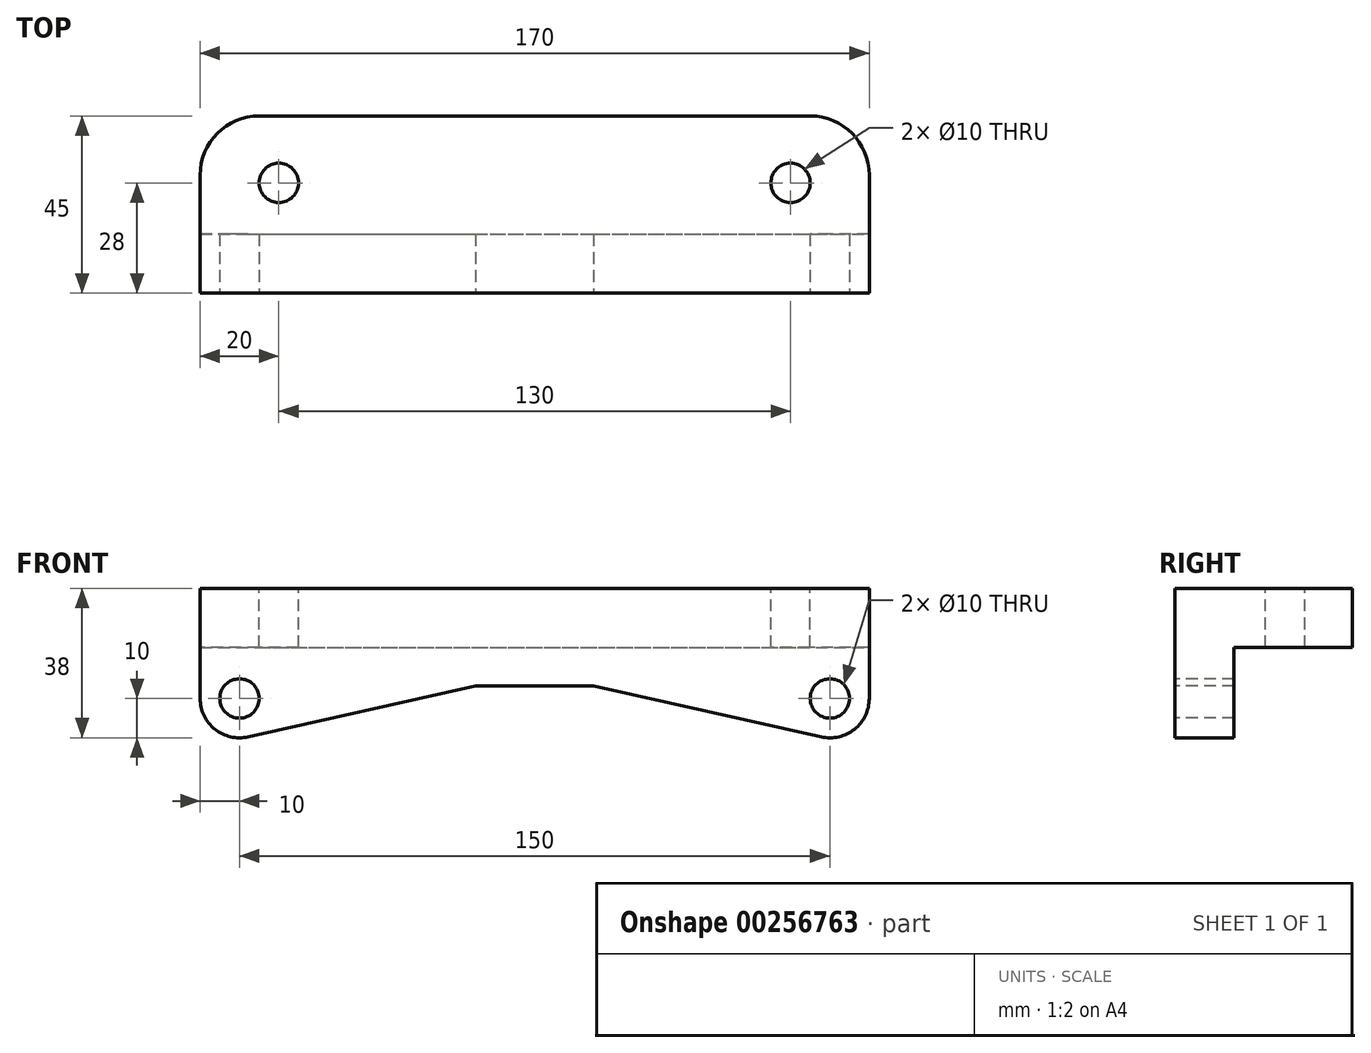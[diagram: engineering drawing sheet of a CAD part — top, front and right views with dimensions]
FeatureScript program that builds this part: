
annotation { "Feature Type Name" : "Feature", "Feature Type Description" : "" }
export const myFeature = defineFeature(function(context is Context, id is Id, definition is map)
    precondition{}
    {
        {
            var Q0;
            Q0=qCreatedBy(makeId("Top.planeOp"),FACE);
            var sketch = newSketch(context, id + "F0", { "sketchPlane" : qUnion([Q0])});
            skLineSegment(sketch, "E0.bottom", {"start": v(-85, 22.5) * mm, "end": v(85, 22.5) * mm});
            skLineSegment(sketch, "E0.top", {"start": v(-85, -22.5) * mm, "end": v(85, -22.5) * mm});
            skLineSegment(sketch, "E0.left", {"start": v(-85, 22.5) * mm, "end": v(-85, -22.5) * mm});
            skLineSegment(sketch, "E0.right", {"start": v(85, 22.5) * mm, "end": v(85, -22.5) * mm});
            skPoint(sketch, "E0.middle", {"position": v(0, 0) * mm});
            skSolve(sketch);
        }
        {
            var Q0;
            Q0=makeQuery(id+"F0.imprint","IMPRINT",FACE,{"disambiguationData":[TD([[makeQuery(id+"F0.imprint","IMPRINT",EDGE,{"derivedFrom":sQuery(id+"F0.wireOp",EDGE,"E0.bottom")}),-1.0]])]});
            extrude(context, id + "F1", {"entities" : qUnion([Q0]), "depth" : 52.5 * mm});
        }
        {
            var Q0;
            Q0=makeQuery(id+"F1.opExtrude","CAP_FACE",FACE,{"disambiguationData":[OSD([sQuery(id+"F0.wireOp",EDGE,"E0.bottom"),sQuery(id+"F0.wireOp",EDGE,"E0.top"),sQuery(id+"F0.wireOp",EDGE,"E0.left"),sQuery(id+"F0.wireOp",EDGE,"E0.right")])],"isStart":false});
            var sketch = newSketch(context, id + "F2", { "sketchPlane" : qUnion([Q0])});
            skLineSegment(sketch, "E1", {"start": v(-65, 5.5) * mm, "end": v(65, 5.5) * mm});
            skSolve(sketch);
        }
        {
            var Q0;
            Q0=sQuery(id+"F2.wireOp",VERTEX,"E1.start");
            var Q1;
            Q1=sQuery(id+"F2.wireOp",VERTEX,"E1.end");
            var Q2;
            Q2=makeQuery(id+"F1.opExtrude","SWEPT_BODY",BODY,{"disambiguationData":[OSD([sQuery(id+"F0.wireOp",EDGE,"E0.bottom"),sQuery(id+"F0.wireOp",EDGE,"E0.top"),sQuery(id+"F0.wireOp",EDGE,"E0.left"),sQuery(id+"F0.wireOp",EDGE,"E0.right")])]});
            hole(context, id + "F3", {"style" : HoleStyle.SIMPLE, "endStyle" : HoleEndStyle.THROUGH, "holeDiameter" : 10 * mm, "tappedDepth" : 12 * mm, "tapClearance" : 3, "startFromSketch" : true, "locations" : qUnion([Q0, Q1]), "scope" : qUnion([Q2])});
        }
        {
            var Q0;
            Q0=makeQuery(id+"F1.opExtrude","SWEPT_FACE",FACE,{"disambiguationData":[OSD([sQuery(id+"F0.wireOp",EDGE,"E0.top")])]});
            var sketch = newSketch(context, id + "F4", { "sketchPlane" : qUnion([Q0])});
            skArc(sketch, "E2", {"start": v(85, 0) * mm, "mid": v(0, 27.5) * mm, "end": v(-85, 0) * mm});
            skLineSegment(sketch, "E3", {"start": v(-85, 0) * mm, "end": v(85, 0) * mm});
            skSolve(sketch);
        }
        {
            var Q0;
            Q0=makeQuery(id+"F4.imprint","IMPRINT",FACE,{"disambiguationData":[TD([[makeQuery(id+"F4.imprint","IMPRINT",EDGE,{"derivedFrom":sQuery(id+"F4.wireOp",EDGE,"E2")}),1.0]])]});
            extrude(context, id + "F5", {"entities" : qUnion([Q0]), "operationType" : NewBodyOperationType.REMOVE, "endBound" : BoundingType.THROUGH_ALL, "oppositeDirection" : true, "depth" : 25 * mm});
        }
        {
            var Q0;
            Q0=makeQuery(id+"F1.opExtrude","SWEPT_FACE",FACE,{"disambiguationData":[OSD([sQuery(id+"F0.wireOp",EDGE,"E0.right")])]});
            var sketch = newSketch(context, id + "F6", { "sketchPlane" : qUnion([Q0])});
            skLineSegment(sketch, "E4.bottom", {"start": v(22.5, 0) * mm, "end": v(-7.5, 0) * mm});
            skLineSegment(sketch, "E4.top", {"start": v(22.5, 37.5) * mm, "end": v(-7.5, 37.5) * mm});
            skLineSegment(sketch, "E4.left", {"start": v(22.5, 0) * mm, "end": v(22.5, 37.5) * mm});
            skLineSegment(sketch, "E4.right", {"start": v(-7.5, 0) * mm, "end": v(-7.5, 37.5) * mm});
            skSolve(sketch);
        }
        {
            var Q0;
            Q0=makeQuery(id+"F6.imprint","IMPRINT",FACE,{"disambiguationData":[TD([[makeQuery(id+"F6.imprint","IMPRINT",EDGE,{"derivedFrom":sQuery(id+"F6.wireOp",EDGE,"E4.bottom")}),-1.0]])]});
            extrude(context, id + "F7", {"entities" : qUnion([Q0]), "operationType" : NewBodyOperationType.REMOVE, "endBound" : BoundingType.THROUGH_ALL, "oppositeDirection" : true, "depth" : 25 * mm});
        }
        {
            var Q0;
            Q0=makeQuery(id+"F1.opExtrude","SWEPT_FACE",FACE,{"disambiguationData":[OSD([sQuery(id+"F0.wireOp",EDGE,"E0.top")])]});
            var sketch = newSketch(context, id + "F8", { "sketchPlane" : qUnion([Q0])});
            skLineSegment(sketch, "E5", {"start": v(-75, 24.5) * mm, "end": v(75, 24.5) * mm});
            skLineSegment(sketch, "E6", {"start": v(0, 0) * mm, "end": v(0, 24.5) * mm});
            skSolve(sketch);
        }
        {
            var Q0;
            Q0=sQuery(id+"F8.wireOp",VERTEX,"E5.start");
            var Q1;
            Q1=sQuery(id+"F8.wireOp",VERTEX,"E5.end");
            var Q2;
            Q2=makeQuery(id+"F1.opExtrude","SWEPT_BODY",BODY,{"disambiguationData":[OSD([sQuery(id+"F0.wireOp",EDGE,"E0.bottom"),sQuery(id+"F0.wireOp",EDGE,"E0.top"),sQuery(id+"F0.wireOp",EDGE,"E0.left"),sQuery(id+"F0.wireOp",EDGE,"E0.right")])]});
            hole(context, id + "F9", {"style" : HoleStyle.SIMPLE, "endStyle" : HoleEndStyle.THROUGH, "holeDiameter" : 10 * mm, "tappedDepth" : 12 * mm, "tapClearance" : 3, "startFromSketch" : true, "locations" : qUnion([Q0, Q1]), "scope" : qUnion([Q2])});
        }
        {
            var Q0;
            Q0=makeQuery(id+"F1.opExtrude","SWEPT_FACE",FACE,{"disambiguationData":[OSD([sQuery(id+"F0.wireOp",EDGE,"E0.top")])]});
            var sketch = newSketch(context, id + "F10", { "sketchPlane" : qUnion([Q0])});
            skArc(sketch, "E7", {"start": v(-85, 24.5) * mm, "mid": v(-81.25, 16.7) * mm, "end": v(-72.8, 14.74) * mm});
            skLineSegment(sketch, "E8", {"start": v(-72.8, 14.74) * mm, "end": v(-31.86, 23.96) * mm});
            skLineSegment(sketch, "E9", {"start": v(-85, 24.5) * mm, "end": v(-85, 0) * mm});
            skLineSegment(sketch, "E10", {"start": v(-85, 0) * mm, "end": v(-31.86, 23.96) * mm});
            skArc(sketch, "E11", {"start": v(72.8, 14.74) * mm, "mid": v(81.25, 16.7) * mm, "end": v(85, 24.5) * mm});
            skLineSegment(sketch, "E12", {"start": v(72.8, 14.74) * mm, "end": v(31.86, 23.96) * mm});
            skLineSegment(sketch, "E13", {"start": v(85, 24.5) * mm, "end": v(85, 0) * mm});
            skLineSegment(sketch, "E14", {"start": v(85, 0) * mm, "end": v(31.86, 23.96) * mm});
            skSolve(sketch);
        }
        {
            var Q0;
            Q0=makeQuery(id+"F10.imprint","IMPRINT",FACE,{"disambiguationData":[TD([[makeQuery(id+"F10.imprint","IMPRINT",EDGE,{"derivedFrom":sQuery(id+"F10.wireOp",EDGE,"E11")}),-1.0]])]});
            var Q1;
            Q1=makeQuery(id+"F10.imprint","IMPRINT",FACE,{"disambiguationData":[TD([[makeQuery(id+"F10.imprint","IMPRINT",EDGE,{"derivedFrom":sQuery(id+"F10.wireOp",EDGE,"E7")}),-1.0]])]});
            extrude(context, id + "F11", {"entities" : qUnion([Q0, Q1]), "operationType" : NewBodyOperationType.REMOVE, "endBound" : BoundingType.THROUGH_ALL, "oppositeDirection" : true, "depth" : 25 * mm});
        }
        {
            var Q0;
            Q0=makeQuery(id+"F1.opExtrude","SWEPT_EDGE",EDGE,{"disambiguationData":[OSD([sQuery(id+"F0.wireOp",EDGE,"E0.bottom"),sQuery(id+"F0.wireOp",EDGE,"E0.right")])]});
            var Q1;
            Q1=makeQuery(id+"F1.opExtrude","SWEPT_EDGE",EDGE,{"disambiguationData":[OSD([sQuery(id+"F0.wireOp",EDGE,"E0.bottom"),sQuery(id+"F0.wireOp",EDGE,"E0.left")])]});
            fillet(context, id + "F12", {"entities" : qUnion([Q0, Q1]), "radius" : 15 * mm, "tangentPropagation" : true, "allowEdgeOverflow" : false});
        }
        {
            var Q0;
            Q0=makeQuery(id+"F1.opExtrude","SWEPT_FACE",FACE,{"disambiguationData":[OSD([sQuery(id+"F0.wireOp",EDGE,"E0.top")])]});
            var sketch = newSketch(context, id + "F13", { "sketchPlane" : qUnion([Q0])});
            skLineSegment(sketch, "E15", {"start": v(-72.8, 14.74) * mm, "end": v(-48.97, 34.74) * mm});
            skLineSegment(sketch, "E16", {"start": v(-48.97, 34.74) * mm, "end": v(48.97, 34.74) * mm});
            skLineSegment(sketch, "E17", {"start": v(48.97, 34.74) * mm, "end": v(72.8, 14.74) * mm});
            skLineSegment(sketch, "E18", {"start": v(72.8, 14.74) * mm, "end": v(-72.8, 14.74) * mm});
            skSolve(sketch);
        }
        {
            var Q0;
            Q0 = qSketchRegion(id + "F13", true);
            var Q1;
            Q1=makeQuery(id+"F7.boolean.opBoolean","COPY",FACE,{"derivedFrom":makeQuery(id+"F7.opExtrude","SWEPT_FACE",FACE,{"disambiguationData":[OSD([sQuery(id+"F6.wireOp",EDGE,"E4.right")])]})});
            extrude(context, id + "F14", {"entities" : qUnion([Q0]), "operationType" : NewBodyOperationType.ADD, "endBound" : BoundingType.UP_TO_SURFACE, "oppositeDirection" : true, "endBoundEntityFace" : qUnion([Q1]), "depth" : 25 * mm});
        }
        {
            var Q0;
            Q0=makeQuery(id+"F1.opExtrude","SWEPT_FACE",FACE,{"disambiguationData":[OSD([sQuery(id+"F0.wireOp",EDGE,"E0.top")])]});
            var sketch = newSketch(context, id + "F15", { "sketchPlane" : qUnion([Q0])});
            skLineSegment(sketch, "E19", {"start": v(-72.8, 14.74) * mm, "end": v(72.8, 14.74) * mm});
            skLineSegment(sketch, "E20", {"start": v(72.8, 14.74) * mm, "end": v(15, 27.74) * mm});
            skLineSegment(sketch, "E21", {"start": v(15, 27.74) * mm, "end": v(-15, 27.74) * mm});
            skLineSegment(sketch, "E22", {"start": v(-15, 27.74) * mm, "end": v(-72.8, 14.74) * mm});
            skLineSegment(sketch, "E23", {"start": v(0, 0) * mm, "end": v(0, 27.74) * mm, "construction": true});
            skSolve(sketch);
        }
        {
            var Q0;
            Q0 = qSketchRegion(id + "F15", true);
            extrude(context, id + "F16", {"entities" : qUnion([Q0]), "operationType" : NewBodyOperationType.REMOVE, "oppositeDirection" : true, "depth" : 25 * mm});
        }
    });
